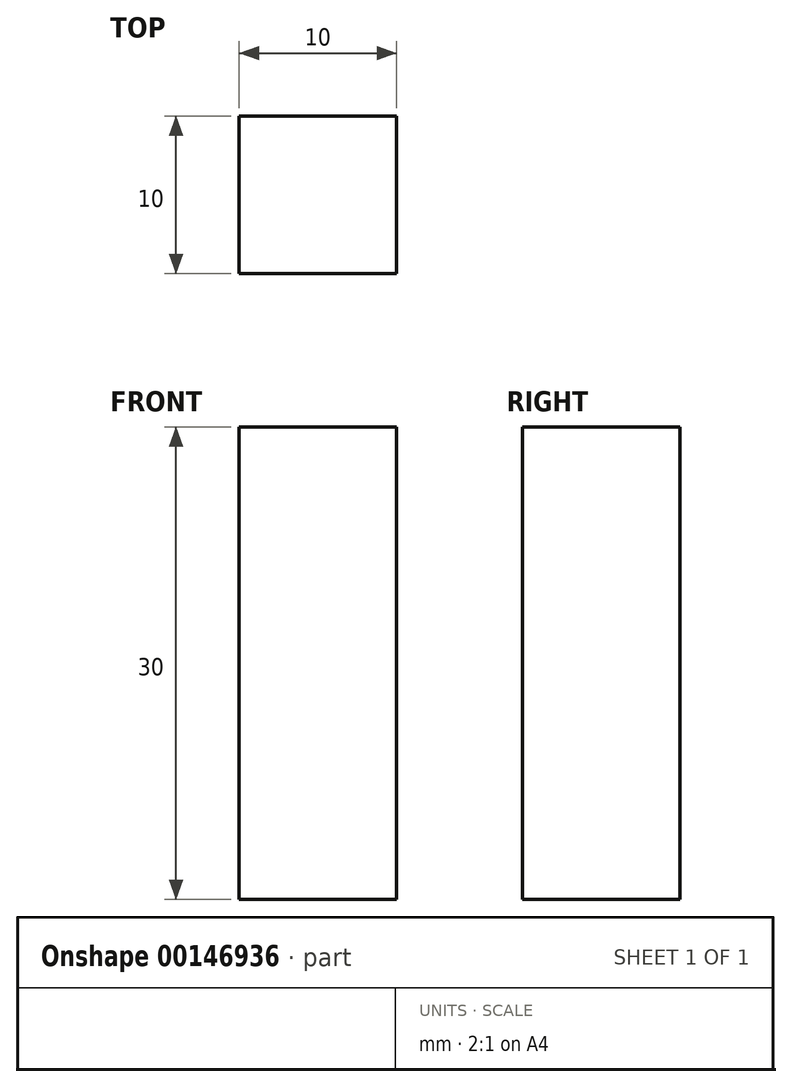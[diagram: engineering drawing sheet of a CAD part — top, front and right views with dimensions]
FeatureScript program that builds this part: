
annotation { "Feature Type Name" : "Feature", "Feature Type Description" : "" }
export const myFeature = defineFeature(function(context is Context, id is Id, definition is map)
    precondition{}
    {
        {
            var Q0;
            Q0=qCreatedBy(makeId("Top.planeOp"),FACE);
            var sketch = newSketch(context, id + "F0", { "sketchPlane" : qUnion([Q0])});
            skLineSegment(sketch, "E0.bottom", {"start": v(0, 0) * mm, "end": v(10, 0) * mm});
            skLineSegment(sketch, "E0.top", {"start": v(0, -10) * mm, "end": v(10, -10) * mm});
            skLineSegment(sketch, "E0.left", {"start": v(0, 0) * mm, "end": v(0, -10) * mm});
            skLineSegment(sketch, "E0.right", {"start": v(10, 0) * mm, "end": v(10, -10) * mm});
            skSolve(sketch);
        }
        {
            var Q0;
            Q0=makeQuery(id+"F0.imprint","IMPRINT",FACE,{"disambiguationData":[TD([[makeQuery(id+"F0.imprint","IMPRINT",EDGE,{"derivedFrom":sQuery(id+"F0.wireOp",EDGE,"E0.bottom")}),-1.0]])]});
            extrude(context, id + "F1", {"entities" : qUnion([Q0]), "depth" : 30 * mm});
        }
    });
